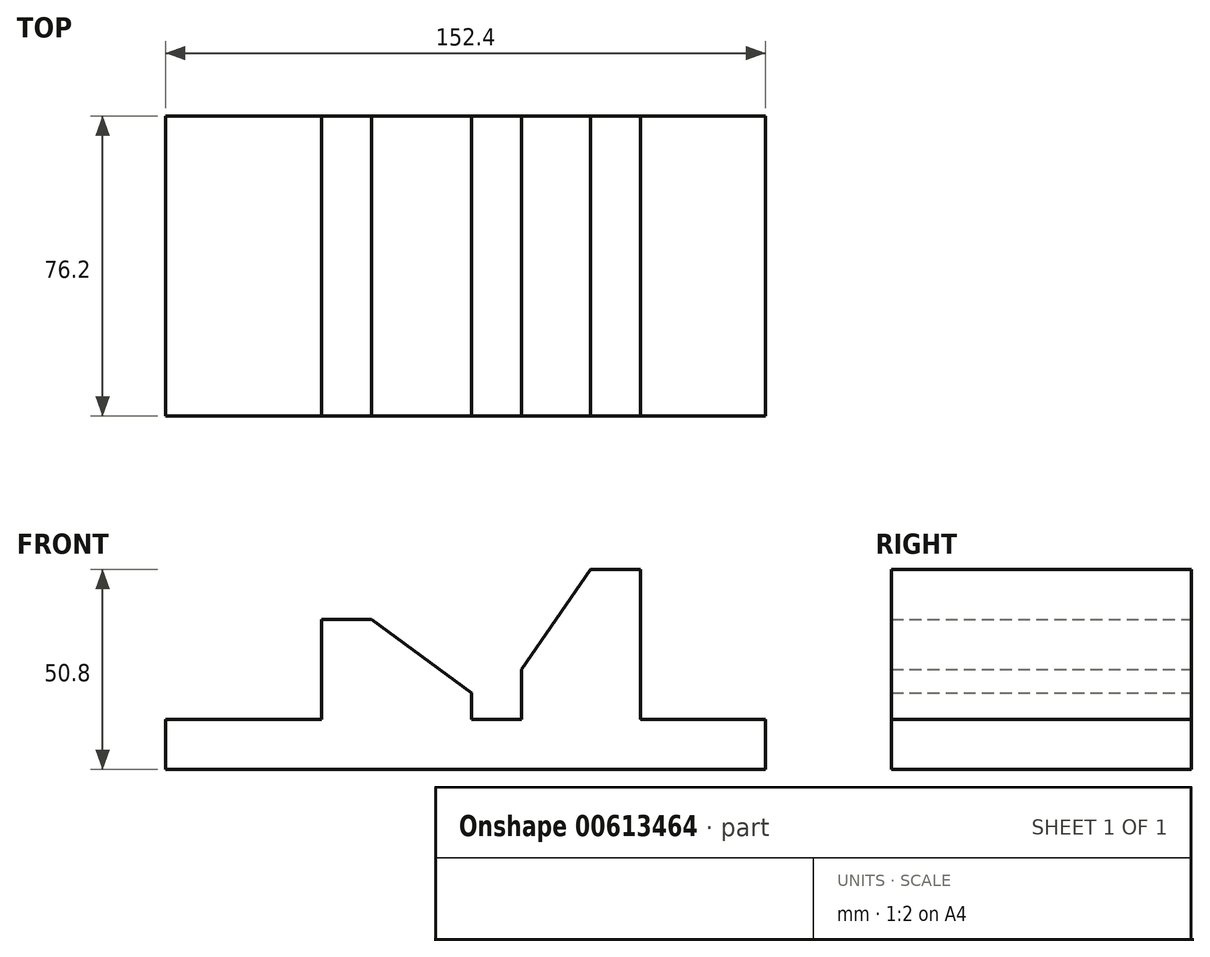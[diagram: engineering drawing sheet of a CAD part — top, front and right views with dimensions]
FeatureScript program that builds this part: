
annotation { "Feature Type Name" : "Feature", "Feature Type Description" : "" }
export const myFeature = defineFeature(function(context is Context, id is Id, definition is map)
    precondition{}
    {
        {
            var Q0;
            Q0=qCreatedBy(makeId("Front.planeOp"),FACE);
            var sketch = newSketch(context, id + "F0", { "sketchPlane" : qUnion([Q0])});
            skLineSegment(sketch, "E0", {"start": v(-69.75, 2.15) * mm, "end": v(82.65, 2.15) * mm});
            skLineSegment(sketch, "E1", {"start": v(82.65, 2.15) * mm, "end": v(82.65, 14.85) * mm});
            skLineSegment(sketch, "E2", {"start": v(82.65, 14.85) * mm, "end": v(50.9, 14.85) * mm});
            skLineSegment(sketch, "E3", {"start": v(50.9, 14.85) * mm, "end": v(50.9, 52.95) * mm});
            skLineSegment(sketch, "E4", {"start": v(50.9, 52.95) * mm, "end": v(38.2, 52.95) * mm});
            skLineSegment(sketch, "E5", {"start": v(38.2, 52.95) * mm, "end": v(20.66, 27.55) * mm});
            skLineSegment(sketch, "E6", {"start": v(20.66, 27.55) * mm, "end": v(20.66, 14.85) * mm});
            skLineSegment(sketch, "E7", {"start": v(20.66, 14.85) * mm, "end": v(7.96, 14.85) * mm});
            skLineSegment(sketch, "E8", {"start": v(7.96, 14.85) * mm, "end": v(7.96, 21.6) * mm});
            skLineSegment(sketch, "E9", {"start": v(7.96, 21.6) * mm, "end": v(-17.44, 40.25) * mm});
            skLineSegment(sketch, "E10", {"start": v(-17.44, 40.25) * mm, "end": v(-30.14, 40.25) * mm});
            skLineSegment(sketch, "E11", {"start": v(-30.14, 40.25) * mm, "end": v(-30.14, 14.85) * mm});
            skLineSegment(sketch, "E12", {"start": v(-30.14, 14.85) * mm, "end": v(-69.75, 14.85) * mm});
            skLineSegment(sketch, "E13", {"start": v(-69.75, 14.85) * mm, "end": v(-69.75, 2.15) * mm});
            skSolve(sketch);
        }
        {
            var Q0;
            Q0 = qSketchRegion(id + "F0", true);
            extrude(context, id + "F1", {"entities" : qUnion([Q0]), "depth" : 76.2 * mm, "offsetDistance" : 25.4 * mm});
        }
    });
